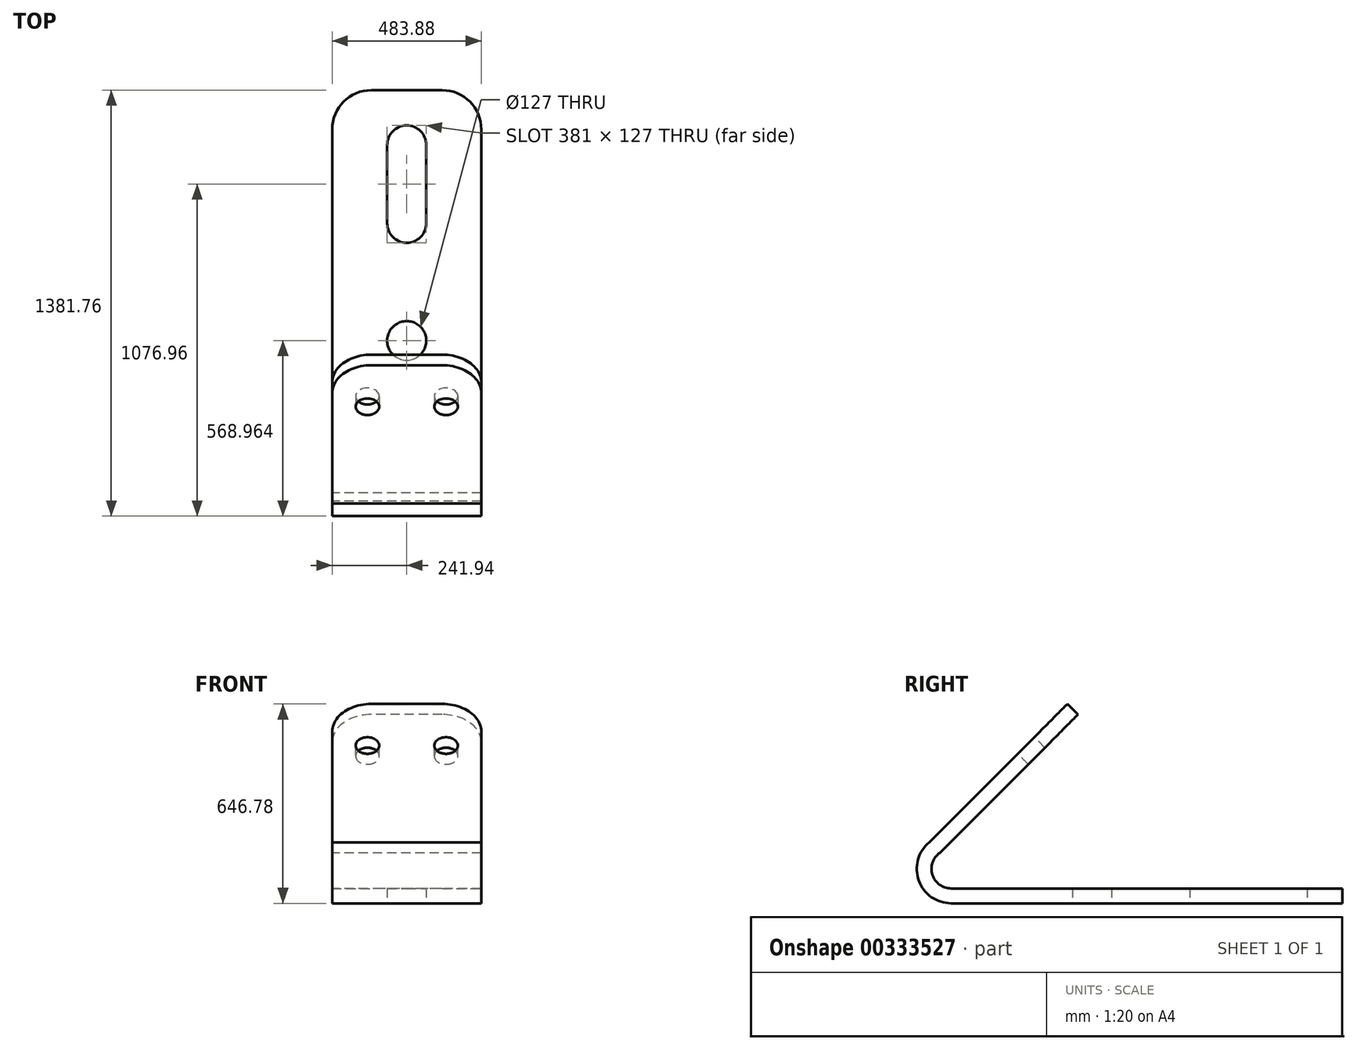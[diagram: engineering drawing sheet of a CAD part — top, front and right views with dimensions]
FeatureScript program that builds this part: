
annotation { "Feature Type Name" : "Feature", "Feature Type Description" : "" }
export const myFeature = defineFeature(function(context is Context, id is Id, definition is map)
    precondition{}
    {
        {
            var Q0;
            Q0=qCreatedBy(makeId("Right.planeOp"),FACE);
            var sketch = newSketch(context, id + "F0", { "sketchPlane" : qUnion([Q0])});
            skLineSegment(sketch, "E0", {"start": v(608.77, 34.35) * mm, "end": v(-661.23, 34.35) * mm});
            skLineSegment(sketch, "E1", {"start": v(-698.46, 149.73) * mm, "end": v(-249.45, 598.74) * mm});
            skLineSegment(sketch, "E2", {"start": v(-249.45, 598.74) * mm, "end": v(-283.57, 632.87) * mm});
            skLineSegment(sketch, "E3", {"start": v(-283.57, 632.87) * mm, "end": v(-732.59, 183.86) * mm});
            skLineSegment(sketch, "E4", {"start": v(608.77, 34.35) * mm, "end": v(608.77, -13.91) * mm});
            skLineSegment(sketch, "E5", {"start": v(608.77, -13.91) * mm, "end": v(-661.23, -13.91) * mm});
            skArc(sketch, "E6", {"start": v(-732.59, 183.86) * mm, "mid": v(-766.35, 59.91) * mm, "end": v(-661.23, -13.91) * mm});
            skArc(sketch, "E7", {"start": v(-698.46, 149.73) * mm, "mid": v(-721.85, 78.48) * mm, "end": v(-661.23, 34.35) * mm});
            skSolve(sketch);
        }
        {
            var Q0;
            Q0 = qSketchRegion(id + "F0", true);
            extrude(context, id + "F1", {"entities" : qUnion([Q0]), "depth" : 483.87 * mm, "offsetDistance" : 25.4 * mm, "symmetric" : true});
        }
        {
            var Q0;
            Q0=makeQuery(id+"F1.opExtrude","CAP_EDGE",EDGE,{"disambiguationData":[OSD([sQuery(id+"F0.wireOp",EDGE,"E2")])],"isStart":false});
            var Q1;
            Q1=makeQuery(id+"F1.opExtrude","CAP_EDGE",EDGE,{"disambiguationData":[OSD([sQuery(id+"F0.wireOp",EDGE,"E2")])],"isStart":true});
            fillet(context, id + "F2", {"entities" : qUnion([Q0, Q1]), "radius" : 127 * mm, "tangentPropagation" : true, "allowEdgeOverflow" : false});
        }
        {
            var Q0;
            Q0=makeQuery(id+"F1.opExtrude","SWEPT_FACE",FACE,{"disambiguationData":[OSD([sQuery(id+"F0.wireOp",EDGE,"E3")])]});
            var sketch = newSketch(context, id + "F3", { "sketchPlane" : qUnion([Q0])});
            skCircle(sketch, "E8", {"center": v(-127.64, 56.49) * mm, "radius": 38.1 * mm});
            skCircle(sketch, "E9", {"center": v(127.64, 56.49) * mm, "radius": 38.1 * mm});
            skSolve(sketch);
        }
        {
            var Q0;
            Q0 = qSketchRegion(id + "F3", true);
            extrude(context, id + "F4", {"entities" : qUnion([Q0]), "operationType" : NewBodyOperationType.REMOVE, "oppositeDirection" : true, "depth" : 68.58 * mm, "offsetDistance" : 25.4 * mm});
        }
        {
            var Q0;
            Q0=makeQuery(id+"F1.opExtrude","CAP_EDGE",EDGE,{"disambiguationData":[OSD([sQuery(id+"F0.wireOp",EDGE,"E4")])],"isStart":false});
            var Q1;
            Q1=makeQuery(id+"F1.opExtrude","CAP_EDGE",EDGE,{"disambiguationData":[OSD([sQuery(id+"F0.wireOp",EDGE,"E4")])],"isStart":true});
            fillet(context, id + "F5", {"entities" : qUnion([Q0, Q1]), "radius" : 127 * mm, "tangentPropagation" : true, "allowEdgeOverflow" : false});
        }
        {
            var Q0;
            Q0=makeQuery(id+"F1.opExtrude","SWEPT_FACE",FACE,{"disambiguationData":[OSD([sQuery(id+"F0.wireOp",EDGE,"E5")])]});
            var sketch = newSketch(context, id + "F6", { "sketchPlane" : qUnion([Q0])});
            skCircle(sketch, "E10", {"center": v(0, 204.03) * mm, "radius": 63.5 * mm});
            skArc(sketch, "E11", {"start": v(-63.48, -178.62) * mm, "mid": v(-0.82, -113.48) * mm, "end": v(63.5, -176.97) * mm});
            skLineSegment(sketch, "E12", {"start": v(63.5, -176.97) * mm, "end": v(63.5, -430.97) * mm});
            skLineSegment(sketch, "E13.MirrorCS", {"start": v(-63.5, -176.97) * mm, "end": v(-63.5, -430.97) * mm});
            skArc(sketch, "E14", {"start": v(-63.5, -430.97) * mm, "mid": v(0, -494.47) * mm, "end": v(63.5, -430.97) * mm});
            skSolve(sketch);
        }
        {
            var Q0;
            Q0 = qSketchRegion(id + "F6", true);
            extrude(context, id + "F7", {"entities" : qUnion([Q0]), "operationType" : NewBodyOperationType.REMOVE, "oppositeDirection" : true, "depth" : 177.8 * mm, "offsetDistance" : 25.4 * mm});
        }
    });
